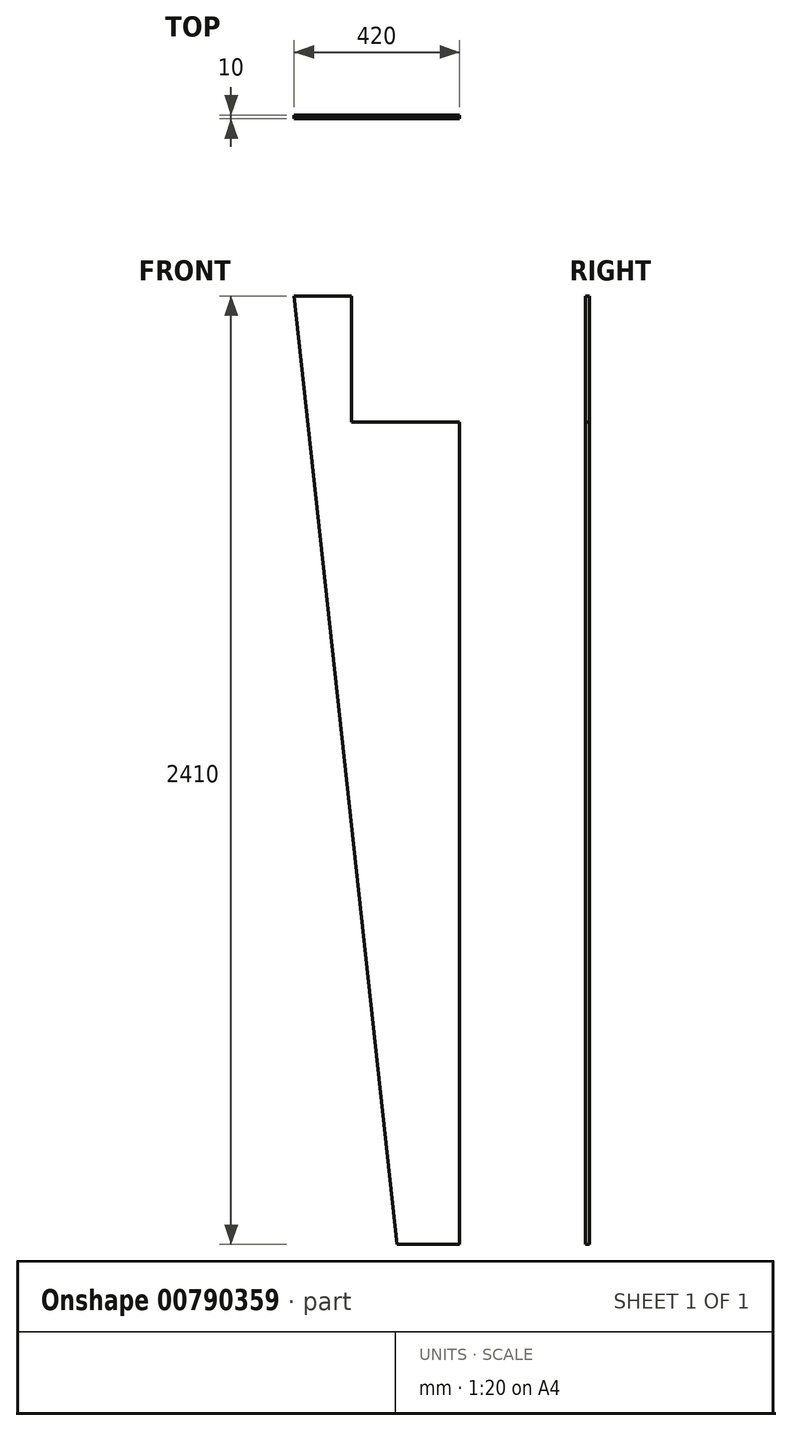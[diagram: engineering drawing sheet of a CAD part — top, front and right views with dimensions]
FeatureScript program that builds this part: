
annotation { "Feature Type Name" : "Feature", "Feature Type Description" : "" }
export const myFeature = defineFeature(function(context is Context, id is Id, definition is map)
    precondition{}
    {
        {
            var Q0;
            Q0=qCreatedBy(makeId("Front.planeOp"),FACE);
            var sketch = newSketch(context, id + "F0", { "sketchPlane" : qUnion([Q0])});
            skLineSegment(sketch, "E0", {"start": v(0, 0) * mm, "end": v(0, 2090) * mm});
            skLineSegment(sketch, "E1", {"start": v(0, 2090) * mm, "end": v(-275, 2090) * mm});
            skLineSegment(sketch, "E2", {"start": v(-275, 2090) * mm, "end": v(-275, 2410) * mm});
            skLineSegment(sketch, "E3", {"start": v(-275, 2410) * mm, "end": v(-420, 2410) * mm});
            skLineSegment(sketch, "E4", {"start": v(0, 0) * mm, "end": v(-159, 0) * mm});
            skLineSegment(sketch, "E5", {"start": v(-420, 2410) * mm, "end": v(-159, 0) * mm});
            skSolve(sketch);
        }
        {
            var Q0;
            Q0=makeQuery(id+"F0.imprint","IMPRINT",FACE,{"disambiguationData":[TD([[makeQuery(id+"F0.imprint","IMPRINT",EDGE,{"derivedFrom":sQuery(id+"F0.wireOp",EDGE,"E0")}),1.0]])]});
            extrude(context, id + "F1", {"entities" : qUnion([Q0]), "depth" : 10 * mm, "offsetDistance" : 25 * mm});
        }
    });
